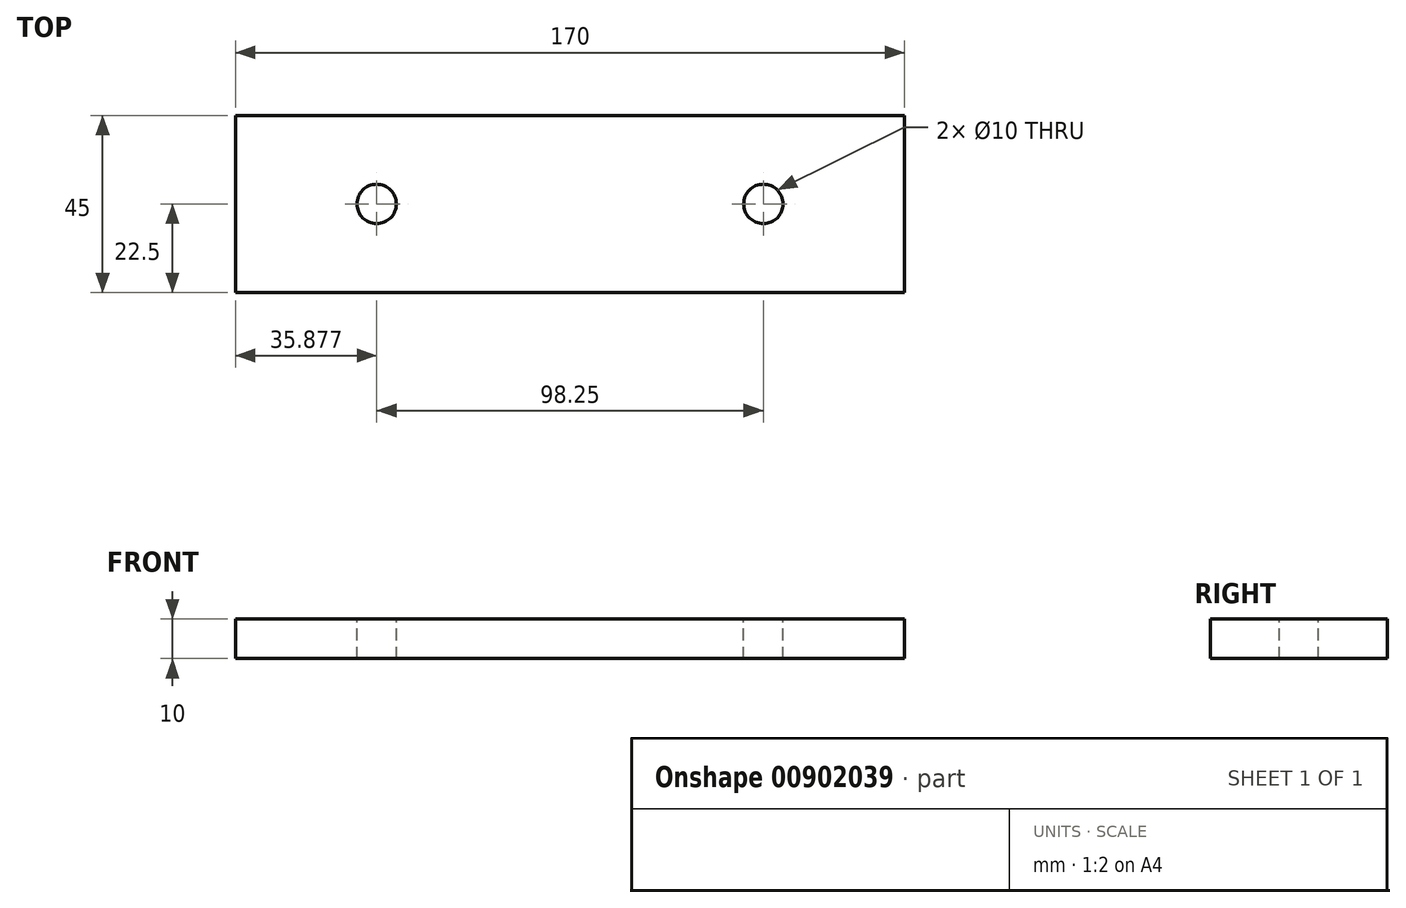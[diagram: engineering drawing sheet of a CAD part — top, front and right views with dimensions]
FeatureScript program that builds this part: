
annotation { "Feature Type Name" : "Feature", "Feature Type Description" : "" }
export const myFeature = defineFeature(function(context is Context, id is Id, definition is map)
    precondition{}
    {
        {
            var Q0;
            Q0=qCreatedBy(makeId("Front.planeOp"),FACE);
            var sketch = newSketch(context, id + "F0", { "sketchPlane" : qUnion([Q0])});
            skLineSegment(sketch, "E0", {"start": v(-69.38, 16.66) * mm, "end": v(100.62, 16.66) * mm});
            skLineSegment(sketch, "E1", {"start": v(100.62, 16.66) * mm, "end": v(100.62, 6.66) * mm});
            skLineSegment(sketch, "E2", {"start": v(100.62, 6.66) * mm, "end": v(-69.38, 6.66) * mm});
            skLineSegment(sketch, "E3", {"start": v(-69.38, 6.66) * mm, "end": v(-69.38, 16.66) * mm});
            skSolve(sketch);
        }
        {
            var Q0;
            Q0=makeQuery(id+"F0.imprint","IMPRINT",FACE,{"disambiguationData":[TD([[makeQuery(id+"F0.imprint","IMPRINT",EDGE,{"derivedFrom":sQuery(id+"F0.wireOp",EDGE,"E0")}),-1.0]])]});
            extrude(context, id + "F1", {"entities" : qUnion([Q0]), "depth" : 45 * mm, "offsetDistance" : 25 * mm});
        }
        {
            var Q0;
            Q0=makeQuery(id+"F1.opExtrude","SWEPT_FACE",FACE,{"disambiguationData":[OSD([sQuery(id+"F0.wireOp",EDGE,"E0")])]});
            var sketch = newSketch(context, id + "F2", { "sketchPlane" : qUnion([Q0])});
            skPoint(sketch, "E4.endSnap0", {"position": v(15.62, -45) * mm});
            skPoint(sketch, "E5", {"position": v(-33.5, -22.5) * mm});
            skPoint(sketch, "E6", {"position": v(64.75, -22.5) * mm});
            skSolve(sketch);
        }
        {
            var Q0;
            Q0=sQuery(id+"F2.wireOp",VERTEX,"E5");
            var Q1;
            Q1=sQuery(id+"F2.wireOp",VERTEX,"E6");
            var Q2;
            Q2=makeQuery(id+"F1.opExtrude","SWEPT_BODY",BODY,{"disambiguationData":[OSD([sQuery(id+"F0.wireOp",EDGE,"E0"),sQuery(id+"F0.wireOp",EDGE,"E1"),sQuery(id+"F0.wireOp",EDGE,"E2"),sQuery(id+"F0.wireOp",EDGE,"E3")])]});
            hole(context, id + "F3", {"style" : HoleStyle.SIMPLE, "endStyle" : HoleEndStyle.THROUGH, "holeDiameter" : 10 * mm, "majorDiameter" : 5 * mm, "isTappedThrough" : true, "tappedDepth" : 12 * mm, "tapClearance" : 3, "startFromSketch" : true, "locations" : qUnion([Q0, Q1]), "scope" : qUnion([Q2])});
        }
    });
